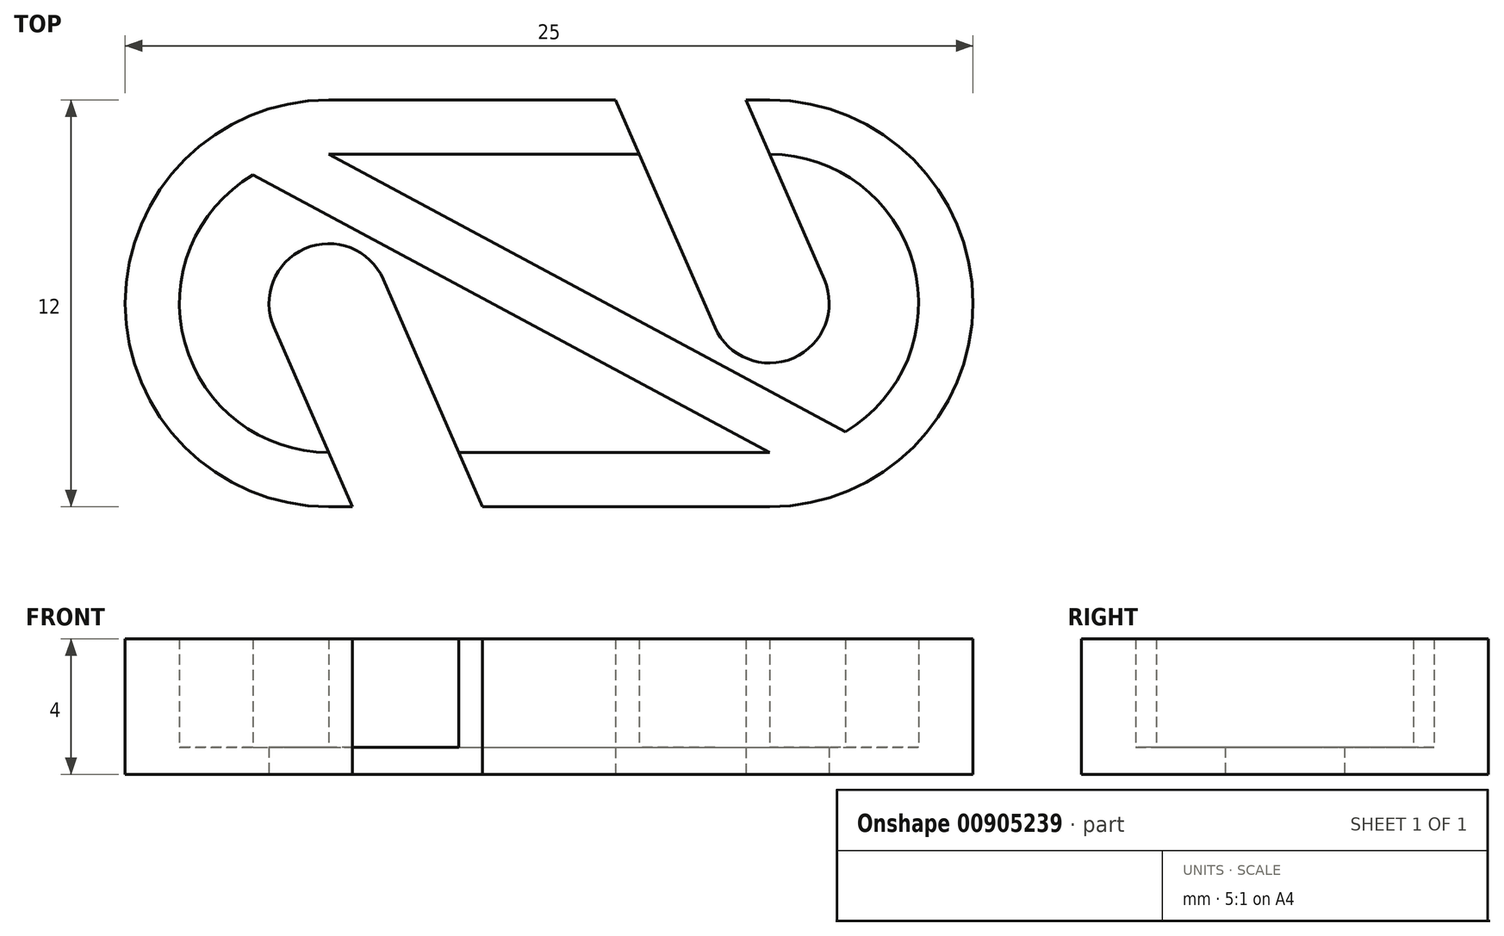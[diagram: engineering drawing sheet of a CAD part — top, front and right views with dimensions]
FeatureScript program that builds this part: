
annotation { "Feature Type Name" : "Feature", "Feature Type Description" : "" }
export const myFeature = defineFeature(function(context is Context, id is Id, definition is map)
    precondition{}
    {
        {
            var Q0;
            Q0=qCreatedBy(makeId("Top.planeOp"),FACE);
            var sketch = newSketch(context, id + "F0", { "sketchPlane" : qUnion([Q0])});
            skArc(sketch, "E0", {"start": v(0, 6) * mm, "mid": v(-6, 0) * mm, "end": v(0, -6) * mm});
            skArc(sketch, "E1", {"start": v(13, -6) * mm, "mid": v(19, 0) * mm, "end": v(13, 6) * mm});
            skArc(sketch, "E2", {"start": v(-2.24, 3.79) * mm, "mid": v(-4.24, -1.16) * mm, "end": v(0, -4.4) * mm});
            skArc(sketch, "E3", {"start": v(15.24, -3.79) * mm, "mid": v(17.24, 1.16) * mm, "end": v(13, 4.4) * mm});
            skLineSegment(sketch, "E4", {"start": v(0, 6) * mm, "end": v(8.46, 6) * mm});
            skLineSegment(sketch, "E5", {"start": v(0, 4.4) * mm, "end": v(9.16, 4.4) * mm});
            skLineSegment(sketch, "E6", {"start": v(3.84, -4.4) * mm, "end": v(13, -4.4) * mm});
            skLineSegment(sketch, "E7", {"start": v(0, -6) * mm, "end": v(0.7, -6) * mm});
            skArc(sketch, "E8", {"start": v(1.61, 0.7) * mm, "mid": v(-0.7, 1.61) * mm, "end": v(-1.61, -0.7) * mm});
            skLineSegment(sketch, "E9", {"start": v(0, -4.4) * mm, "end": v(-1.61, -0.7) * mm});
            skLineSegment(sketch, "E10", {"start": v(13, 4.4) * mm, "end": v(14.61, 0.7) * mm});
            skArc(sketch, "E11.trimOffspring", {"start": v(11.39, -0.7) * mm, "mid": v(13.7, -1.61) * mm, "end": v(14.61, 0.7) * mm});
            skLineSegment(sketch, "E12", {"start": v(-2.24, 3.79) * mm, "end": v(13, -4.4) * mm});
            skLineSegment(sketch, "E13", {"start": v(0, 4.4) * mm, "end": v(15.24, -3.79) * mm});
            skLineSegment(sketch, "E14", {"start": v(-0.8, -2.55) * mm, "end": v(0.7, -6) * mm});
            skLineSegment(sketch, "E15.trimOffspring", {"start": v(4.54, -6) * mm, "end": v(13, -6) * mm});
            skLineSegment(sketch, "E16.trimOffspring", {"start": v(12.3, 6) * mm, "end": v(13, 6) * mm});
            skLineSegment(sketch, "E17", {"start": v(13, 4.4) * mm, "end": v(12.3, 6) * mm});
            skLineSegment(sketch, "E18", {"start": v(11.39, -0.7) * mm, "end": v(8.46, 6) * mm});
            skPoint(sketch, "E19.orphan", {"position": v(11.9, 6) * mm});
            skLineSegment(sketch, "E20", {"start": v(1.61, 0.7) * mm, "end": v(4.54, -6) * mm});
            skSolve(sketch);
        }
        {
            var Q0;
            Q0=makeQuery(id+"F0.imprint","IMPRINT",FACE,{"disambiguationData":[TD([[makeQuery(id+"F0.imprint","IMPRINT",EDGE,{"derivedFrom":sQuery(id+"F0.wireOp",EDGE,"BtGibEIR-U8U0-MmIt-Td02-Rgo3iUXSvpdN.bottom")}),-1.0]])]});
            var Q1;
            Q1=makeQuery(id+"F0.imprint","IMPRINT",FACE,{"disambiguationData":[TD([[makeQuery(id+"F0.imprint","IMPRINT",EDGE,{"derivedFrom":sQuery(id+"F0.wireOp",EDGE,"E0")}),1.0]])]});
            var Q2;
            Q2=makeQuery(id+"F0.imprint","IMPRINT",FACE,{"disambiguationData":[TD([[makeQuery(id+"F0.imprint","IMPRINT",EDGE,{"derivedFrom":sQuery(id+"F0.wireOp",EDGE,"E1")}),1.0]])]});
            extrude(context, id + "F1", {"entities" : qUnion([Q0, Q1, Q2]), "depth" : 4 * mm, "offsetDistance" : 25 * mm});
        }
        {
            var Q0;
            {var subQ2=sQuery(id+"F0.wireOp",EDGE,"E2");Q0=makeQuery(id+"F0.imprint","IMPRINT",FACE,{"disambiguationData":[TD([[makeQuery(id+"F0.imprint","IMPRINT",EDGE,{"derivedFrom":subQ2}),1.0]])]});}
            var Q1;
            {var subQ1=sQuery(id+"F0.wireOp",EDGE,"E3");Q1=makeQuery(id+"F0.imprint","IMPRINT",FACE,{"disambiguationData":[TD([[makeQuery(id+"F0.imprint","IMPRINT",EDGE,{"derivedFrom":subQ1}),1.0]])]});}
            extrude(context, id + "F2", {"entities" : qUnion([Q0, Q1]), "operationType" : NewBodyOperationType.ADD, "depth" : .8 * mm, "offsetDistance" : 25 * mm});
        }
    });
